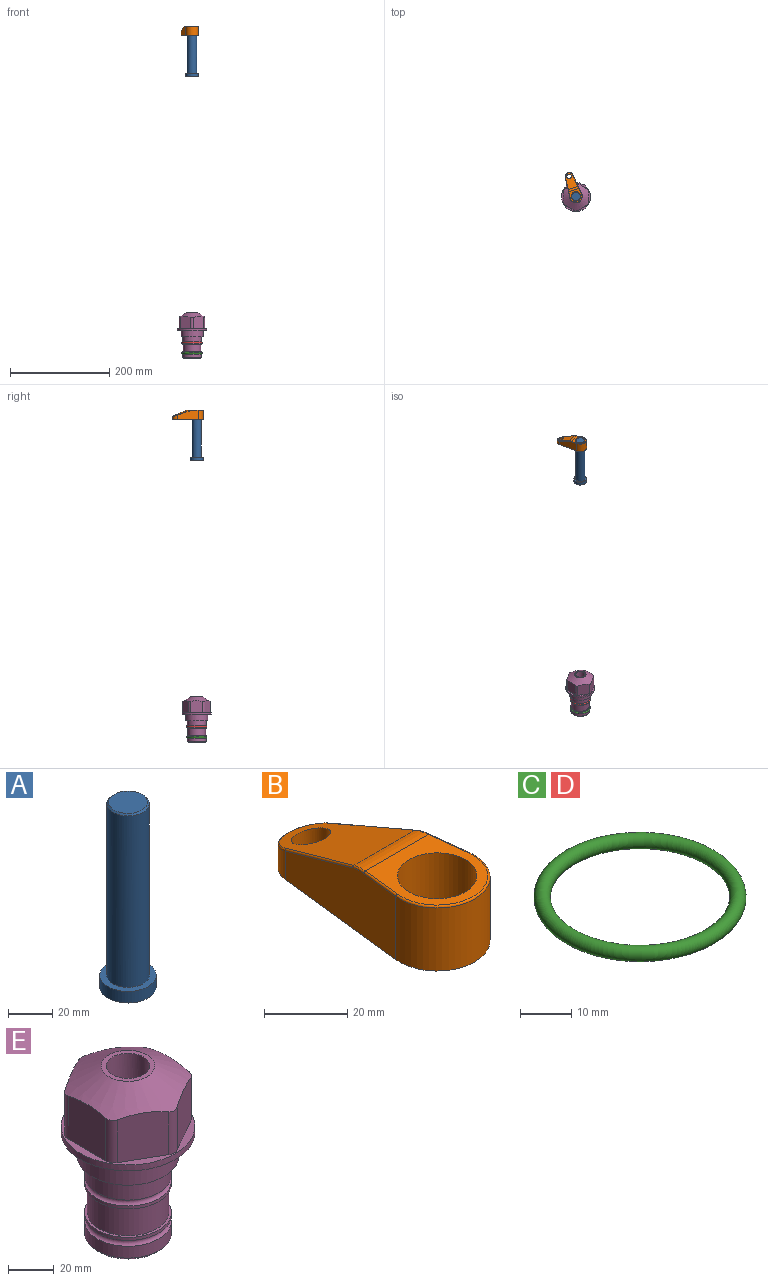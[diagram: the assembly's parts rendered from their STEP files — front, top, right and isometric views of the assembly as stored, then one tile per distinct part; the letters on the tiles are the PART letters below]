
ASSEMBLY  parts=5 mates=3
PART A: 6 faces, bbox 25.4x25.4x101.6 mm
  f0: plane 17.46x17.46mm, normal (0,0,1), area 239.5mm2, adj f5
  f1: plane 25.4x25.4mm, normal (0,0,-1), area 506.7mm2, adj f2
  f2: cylinder r=12.7mm len=25.4mm, axis (0,0,1), area 506.7mm2, adj f1,f3
  f3: plane 25.4x25.4mm, normal (0,0,1), area 221.7mm2, adj f2,f4
  f4: cylinder r=9.53mm len=94.46mm, axis (0,0,1), area 5653mm2, adj f3,f5
  f5: cone r=8.73mm half-angle=45deg, axis (0,0,-1), area 64.4mm2, adj f0,f4
PART B: 44 faces, bbox 27.5x64.5x19.1 mm
  f0: plane 2.3x0.95mm, normal (0,0,-1), area 1mm2, adj f25,f30,f34
  f1: plane 63.5x25.4mm, normal (0,0,-1), area 561.7mm2, adj f2,f3,f4,f5,f6,f7,f19,f20
  f2: cylinder r=12.7mm len=25.4mm, axis (0,0,-1), area 792.2mm2, adj f1,f3,f5,f13
  f3: plane 42.33x18.54mm, normal (0.99,0.11,0), area 647mm2, adj f1,f2,f4,f11,f12,f14
  f4: cylinder r=7.94mm len=15.78mm, axis (0,0,-1), area 158.6mm2, adj f1,f3,f5,f16
  f5: plane 42.33x18.54mm, normal (-0.99,0.11,0), area 647mm2, adj f1,f2,f4,f15,f17,f18
  f6: cylinder r=9.53mm len=19.05mm, axis (0,0,-1), area 1140.1mm2, adj f1,f8
  f7: cylinder r=4.76mm len=10.98mm, axis (0,0,-1), area 276.1mm2, adj f1,f9
  f8: plane 25.83x24.38mm, normal (0,0,1), area 262.2mm2, adj f6,f10,f11,f13,f15
  f9: plane 32.49x20.55mm, normal (0,0.34,0.94), area 489.9mm2, adj f7,f10,f14,f16,f18
  f10: cylinder r=12.7mm len=21.49mm, axis (-1,0,0), area 93.2mm2, adj f8,f9,f12,f17
  f11: cylinder r=0.51mm len=12.34mm, axis (0.11,-0.99,0), area 9.9mm2, adj f3,f8,f12,f13
  f12: bspline ~7.62x1.64mm, area 3.5mm2, adj f3,f10,f11,f14
  f13: torus R=12.19mm, axis (0,0,1), area 33.6mm2, adj f2,f8,f11,f15
  f14: cylinder r=0.51mm len=26.01mm, axis (0.1,-0.93,0.34), area 21.6mm2, adj f3,f9,f12,f16
  f15: cylinder r=0.51mm len=12.34mm, axis (0.11,0.99,0), area 9.9mm2, adj f5,f8,f13,f17
  f16: bspline ~15.78x7.05mm, area 15.7mm2, adj f4,f9,f14,f18
  f17: bspline ~7.62x1.64mm, area 3.5mm2, adj f5,f10,f15,f18
  f18: cylinder r=0.51mm len=26.01mm, axis (0.1,0.93,-0.34), area 21.6mm2, adj f5,f9,f16,f17
  f19: plane 21.6x14.29mm, normal (-0.99,-0.11,0), area 242.6mm2, adj f1,f26,f28,f34,f36,f38
  f20: plane 21.6x14.29mm, normal (0.99,-0.11,0), area 242.6mm2, adj f1,f27,f29,f37,f39,f41
  f21: cylinder r=12.7mm len=14.29mm, axis (0,0,-1), area 173.2mm2, adj f1,f26,f27,f30,f31,f33
  f22: cylinder r=7.94mm len=7.63mm, axis (0,0,-1), area 53.8mm2, adj f1,f28,f29,f42
  f23: plane 2.3x0.95mm, normal (0,0,-1), area 1mm2, adj f25,f33,f37
  f24: plane 17.94x12.32mm, normal (0,-0.34,-0.94), area 191.2mm2, adj f25,f38,f41,f42
  f25: cylinder r=9.53mm len=12.93mm, axis (-1,0,0), area 37.5mm2, adj f0,f23,f24,f31,f36,f39
  f26: cylinder r=1.59mm len=14.29mm, axis (0,0,-1), area 49mm2, adj f1,f19,f21,f32
  f27: cylinder r=1.59mm len=14.29mm, axis (0,0,-1), area 49mm2, adj f1,f20,f21,f35
  f28: cylinder r=1.59mm len=7.28mm, axis (0,0,-1), area 22.1mm2, adj f1,f19,f22,f40
  f29: cylinder r=1.59mm len=7.28mm, axis (0,0,-1), area 22.1mm2, adj f1,f20,f22,f43
  f30: torus R=14.29mm, axis (0,0,1), area 5.8mm2, adj f0,f21,f31,f32
  f31: bspline ~11.06x2.73mm, area 20.8mm2, adj f21,f25,f30,f33
  f32: sphere r=1.59mm, area 5.4mm2, adj f26,f30,f34
  f33: torus R=14.29mm, axis (0,0,1), area 5.8mm2, adj f21,f23,f31,f35
  f34: cylinder r=1.59mm len=1.68mm, axis (-0.11,0.99,0), area 2.4mm2, adj f0,f19,f32,f36
  f35: sphere r=1.59mm, area 5.4mm2, adj f27,f33,f37
  f36: bspline ~5.82x2.33mm, area 7.7mm2, adj f19,f25,f34,f38
  f37: cylinder r=1.59mm len=1.68mm, axis (0.11,0.99,0), area 2.4mm2, adj f20,f23,f35,f39
  f38: cylinder r=1.59mm len=18.33mm, axis (0.1,-0.93,0.34), area 46.7mm2, adj f19,f24,f36,f40
  f39: bspline ~5.82x2.33mm, area 7.7mm2, adj f20,f25,f37,f41
  f40: sphere r=1.59mm, area 3.6mm2, adj f28,f38,f42
  f41: cylinder r=1.59mm len=18.33mm, axis (0.1,0.93,-0.34), area 46.7mm2, adj f20,f24,f39,f43
  f42: bspline ~8.31x1.84mm, area 15.3mm2, adj f22,f24,f40,f43
  f43: sphere r=1.59mm, area 3.6mm2, adj f29,f41,f42
PART C: 1 faces, bbox 44.7x44.7x3.2 mm
  f0: torus R=19.05mm, axis (0,0,1), area 1193.9mm2
PART D: same geometry as C
PART E: 36 faces, bbox 58.7x58.7x91.2 mm
  f0: cylinder r=17.78mm len=35.56mm, axis (0,0,1), area 1670.8mm2, adj f23,f24,f31
  f1: cylinder r=19.05mm len=38.1mm, axis (0,0,1), area 1191.9mm2, adj f26,f27,f30
  f2: plane 58.66x58.66mm, normal (0,0,-1), area 1150.6mm2, adj f3,f28
  f3: cylinder r=29.33mm len=58.66mm, axis (0,0,-1), area 585.1mm2, adj f2,f4
  f4: plane 58.66x58.66mm, normal (0,0,1), area 475.9mm2, adj f3,f5,f6,f7,f8,f9,f10,f11
  f5: plane 24.5x20.32mm, normal (-0.5,0.87,0), area 562.8mm2, adj f4,f15,f16,f17
  f6: plane 24.5x20.32mm, normal (0.5,0.87,0), area 562.8mm2, adj f4,f14,f15,f17
  f7: plane 24.5x23.48mm, normal (1,0,0), area 562.8mm2, adj f4,f13,f14,f17
  f8: plane 24.5x20.32mm, normal (0.5,-0.87,0), area 562.8mm2, adj f4,f12,f13,f17
  f9: plane 24.5x20.32mm, normal (-0.5,-0.87,0), area 562.8mm2, adj f4,f11,f12,f17
  f10: plane 24.5x23.48mm, normal (-1,0,0), area 562.8mm2, adj f4,f11,f16,f17
  f11: cylinder r=5.08mm len=23.01mm, axis (0,0,-1), area 121.2mm2, adj f4,f9,f10,f17
  f12: cylinder r=5.08mm len=23.01mm, axis (0,0,-1), area 121.2mm2, adj f4,f8,f9,f17
  f13: cylinder r=5.08mm len=23.01mm, axis (0,0,-1), area 121.2mm2, adj f4,f7,f8,f17
  f14: cylinder r=5.08mm len=23.01mm, axis (0,0,-1), area 121.2mm2, adj f4,f6,f7,f17
  f15: cylinder r=5.08mm len=23.01mm, axis (0,0,-1), area 121.2mm2, adj f4,f5,f6,f17
  f16: cylinder r=5.08mm len=23.01mm, axis (0,0,-1), area 121.2mm2, adj f4,f5,f10,f17
  f17: cone r=11.73mm half-angle=60deg, axis (0,0,-1), area 2071.8mm2, adj f5,f6,f7,f8,f9,f10,f11,f12
  f18: plane 23.46x23.46mm, normal (0,0,1), area 147.4mm2, adj f17,f35
  f19: plane 34.93x34.93mm, normal (0,0,-1), area 958mm2, adj f29
  f20: cylinder r=19.05mm len=38.1mm, axis (0,0,1), area 760.1mm2, adj f21,f29
  f21: torus R=19.05mm, axis (0,0,1), area 565.3mm2, adj f20,f22
  f22: cylinder r=19.05mm len=38.1mm, axis (0,0,1), area 190mm2, adj f21,f23
  f23: plane 38.1x38.1mm, normal (0,0,1), area 146.9mm2, adj f0,f22
  f24: plane 38.1x38.1mm, normal (0,0,-1), area 146.9mm2, adj f0,f25
  f25: cylinder r=19.05mm len=38.1mm, axis (0,0,1), area 190mm2, adj f24,f26
  f26: torus R=19.05mm, axis (0,0,1), area 565.3mm2, adj f1,f25
  f27: plane 44.45x44.45mm, normal (0,0,-1), area 411.7mm2, adj f1,f28
  f28: cylinder r=22.23mm len=44.45mm, axis (0,0,1), area 1773.5mm2, adj f2,f27
  f29: cone r=19.05mm half-angle=45deg, axis (0,0,1), area 257.5mm2, adj f19,f20
  f30: cylinder r=3.17mm len=6.75mm, axis (-1,0,0), area 128mm2, adj f1,f33
  f31: cylinder r=3.17mm len=6.35mm, axis (-1,0,0), area 102.5mm2, adj f0,f33
  f32: plane 25.4x25.4mm, normal (0,0,1), area 506.7mm2, adj f33
  f33: cylinder r=12.7mm len=66.42mm, axis (0,0,-1), area 5236.2mm2, adj f30,f31,f32,f34
  f34: cone r=9.53mm half-angle=30deg, axis (0,0,-1), area 443.4mm2, adj f33,f35
  f35: cylinder r=9.53mm len=19.05mm, axis (0,0,-1), area 849mm2, adj f18,f34
PLACE A rot(axis=(0,0,1),108.9deg) t=(0,0,540.82)mm
PLACE B rot(axis=(0,0,1),18.9deg) t=(0,0,595.43)mm
PLACE C t=(0,0,-21.59)mm
PLACE D at identity
PLACE E at identity fixed
MATE fastened C.f0 <-> E.f0  axis (0,0,1) through (0,0,-46.1)mm
MATE cylindrical A.f2 <-> E.f0  axis (0,0,1) through (0,0,566.45)mm
MATE fastened B.f2 <-> A.f2  axis (0,0,1) through (0,0,614.48)mm
